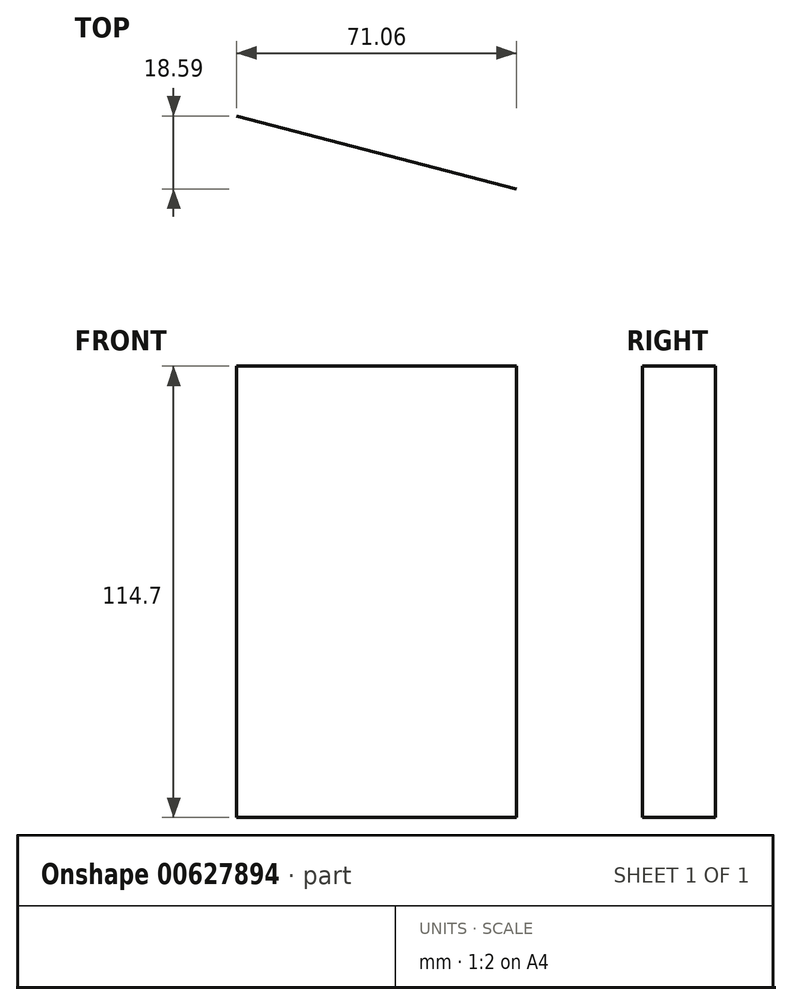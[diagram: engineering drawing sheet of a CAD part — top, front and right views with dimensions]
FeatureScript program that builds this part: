
annotation { "Feature Type Name" : "Feature", "Feature Type Description" : "" }
export const myFeature = defineFeature(function(context is Context, id is Id, definition is map)
    precondition{}
    {
        {
            var Q0;
            Q0=qCreatedBy(makeId("Top.planeOp"),FACE);
            var sketch = newSketch(context, id + "F0", { "sketchPlane" : qUnion([Q0])});
            skCircle(sketch, "E0.cCircle", {"center": v(-103.8, -41.69) * mm, "radius": 97.3 * mm, "construction": true});
            skLineSegment(sketch, "E0.0", {"start": v(-53.87, 41.81) * mm, "end": v(-6.52, -43.18) * mm});
            skLineSegment(sketch, "E0.1", {"start": v(-6.52, -43.18) * mm, "end": v(-56.46, -126.68) * mm});
            skLineSegment(sketch, "E0.2", {"start": v(-56.46, -126.68) * mm, "end": v(-153.74, -125.2) * mm});
            skLineSegment(sketch, "E0.3", {"start": v(-153.74, -125.2) * mm, "end": v(-201.09, -40.2) * mm});
            skLineSegment(sketch, "E0.4", {"start": v(-201.09, -40.2) * mm, "end": v(-151.15, 43.3) * mm});
            skLineSegment(sketch, "E0.5", {"start": v(-151.15, 43.3) * mm, "end": v(-53.87, 41.81) * mm});
            skCircle(sketch, "E1.cCircle", {"center": v(-103.8, -91.98) * mm, "radius": 73.45 * mm, "construction": true});
            skLineSegment(sketch, "E1.0", {"start": v(-123.23, -21.15) * mm, "end": v(-52.17, -39.74) * mm});
            skLineSegment(sketch, "E1.1", {"start": v(-52.17, -39.74) * mm, "end": v(-32.74, -110.57) * mm});
            skLineSegment(sketch, "E1.2", {"start": v(-32.74, -110.57) * mm, "end": v(-84.38, -162.82) * mm});
            skLineSegment(sketch, "E1.3", {"start": v(-84.38, -162.82) * mm, "end": v(-155.44, -144.23) * mm});
            skLineSegment(sketch, "E1.4", {"start": v(-155.44, -144.23) * mm, "end": v(-174.87, -73.4) * mm});
            skLineSegment(sketch, "E1.5", {"start": v(-174.87, -73.4) * mm, "end": v(-123.23, -21.15) * mm});
            skCircle(sketch, "E2.cCircle", {"center": v(0, -206.72) * mm, "radius": 95.11 * mm, "construction": true});
            skLineSegment(sketch, "E2.0", {"start": v(-84.38, -162.82) * mm, "end": v(-4.17, -111.7) * mm});
            skLineSegment(sketch, "E2.1", {"start": v(-4.17, -111.7) * mm, "end": v(80.2, -155.6) * mm});
            skLineSegment(sketch, "E2.2", {"start": v(80.2, -155.6) * mm, "end": v(84.38, -250.62) * mm});
            skLineSegment(sketch, "E2.3", {"start": v(84.38, -250.62) * mm, "end": v(4.17, -301.74) * mm});
            skLineSegment(sketch, "E2.4", {"start": v(4.17, -301.74) * mm, "end": v(-80.2, -257.84) * mm});
            skLineSegment(sketch, "E2.5", {"start": v(-80.2, -257.84) * mm, "end": v(-84.38, -162.82) * mm});
            skSolve(sketch);
        }
        {
            var Q0;
            Q0=sQuery(id+"F0.wireOp",EDGE,"E1.0");
            extrude(context, id + "F1", {"bodyType" : ToolBodyType.SURFACE, "surfaceEntities" : qUnion([Q0]), "depth" : 114.7 * mm, "offsetDistance" : 25.4 * mm});
        }
    });
